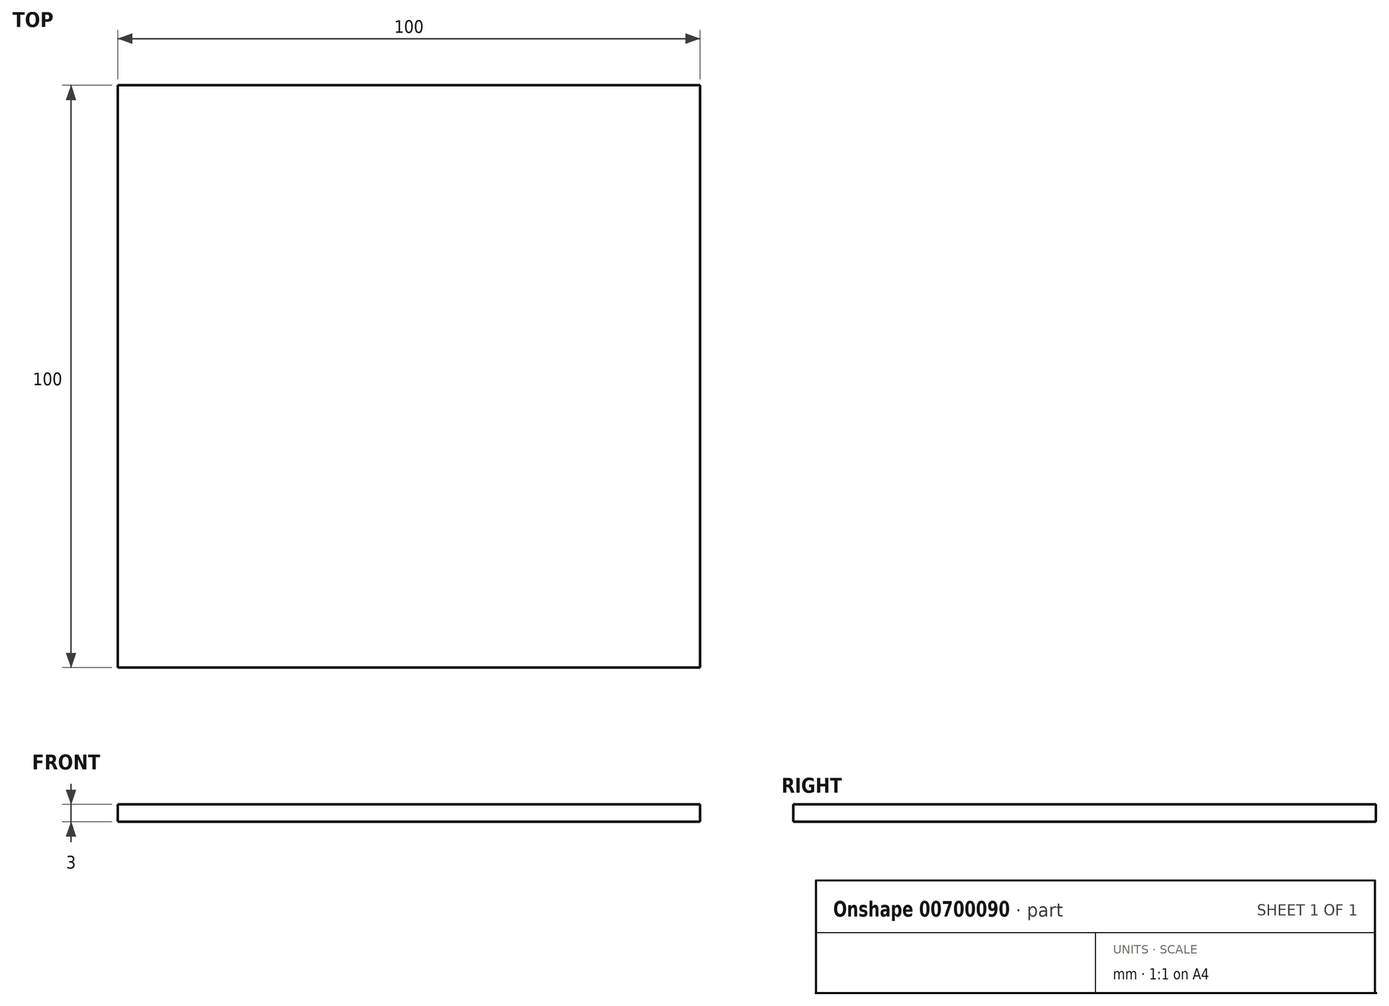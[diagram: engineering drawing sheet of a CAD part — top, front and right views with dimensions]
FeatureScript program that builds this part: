
annotation { "Feature Type Name" : "Feature", "Feature Type Description" : "" }
export const myFeature = defineFeature(function(context is Context, id is Id, definition is map)
    precondition{}
    {
        {
            var Q0;
            Q0=qCreatedBy(makeId("Top.planeOp"),FACE);
            var sketch = newSketch(context, id + "F0", { "sketchPlane" : qUnion([Q0])});
            skLineSegment(sketch, "E0.bottom", {"start": v(50, 50) * mm, "end": v(-50, 50) * mm});
            skLineSegment(sketch, "E0.top", {"start": v(50, -50) * mm, "end": v(-50, -50) * mm});
            skLineSegment(sketch, "E0.left", {"start": v(50, 50) * mm, "end": v(50, -50) * mm});
            skLineSegment(sketch, "E0.right", {"start": v(-50, 50) * mm, "end": v(-50, -50) * mm});
            skPoint(sketch, "E0.middle", {"position": v(0, 0) * mm});
            skSolve(sketch);
        }
        {
            var Q0;
            Q0 = qSketchRegion(id + "F0", true);
            extrude(context, id + "F1", {"entities" : qUnion([Q0]), "depth" : 3 * mm, "offsetDistance" : 25 * mm});
        }
    });
